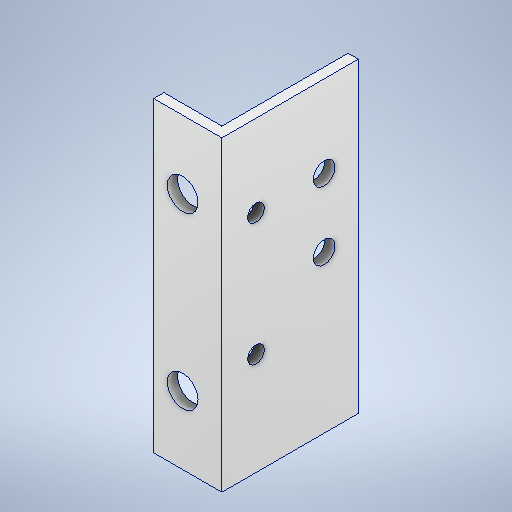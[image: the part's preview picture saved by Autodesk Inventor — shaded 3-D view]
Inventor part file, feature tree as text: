
AUTODESK INVENTOR PART (.ipt)
format: ipt  version: 2025 (Build 290162000, 162)  size: 286,208 bytes
history: native  units: mm
features: sketch x4, hole x3, projected_geometry x3, other x1, extrude x1
ambient origin geometry x8: Origin, YZ Plane, XZ Plane, XY Plane, X Axis, Y Axis, Z Axis, Center Point
bodies: Body1 (feature_tree)
feature tree (12):
  other  "Těleso1"
  extrude  "Vysunutí1"  Depth=20.0mm
  hole  "Díra1"  [1 undecoded]
  hole  "Díra2"  [1 undecoded]
  hole  "Díra3"  [1 undecoded]
  sketch  "Náčrt1"
  sketch  "Náčrt2"
  projected_geometry  "Promítnutá smyčka1"
  sketch  "Náčrt3"
  projected_geometry  "Promítnutá smyčka2"
  sketch  "Náčrt4"
  projected_geometry  "Promítnutá smyčka3"
note: 3 required parameter values undecoded (feature->parameter linkage not recoverable at this tier; creation-order binding heuristic only, values carry confidence <= 0.55)
